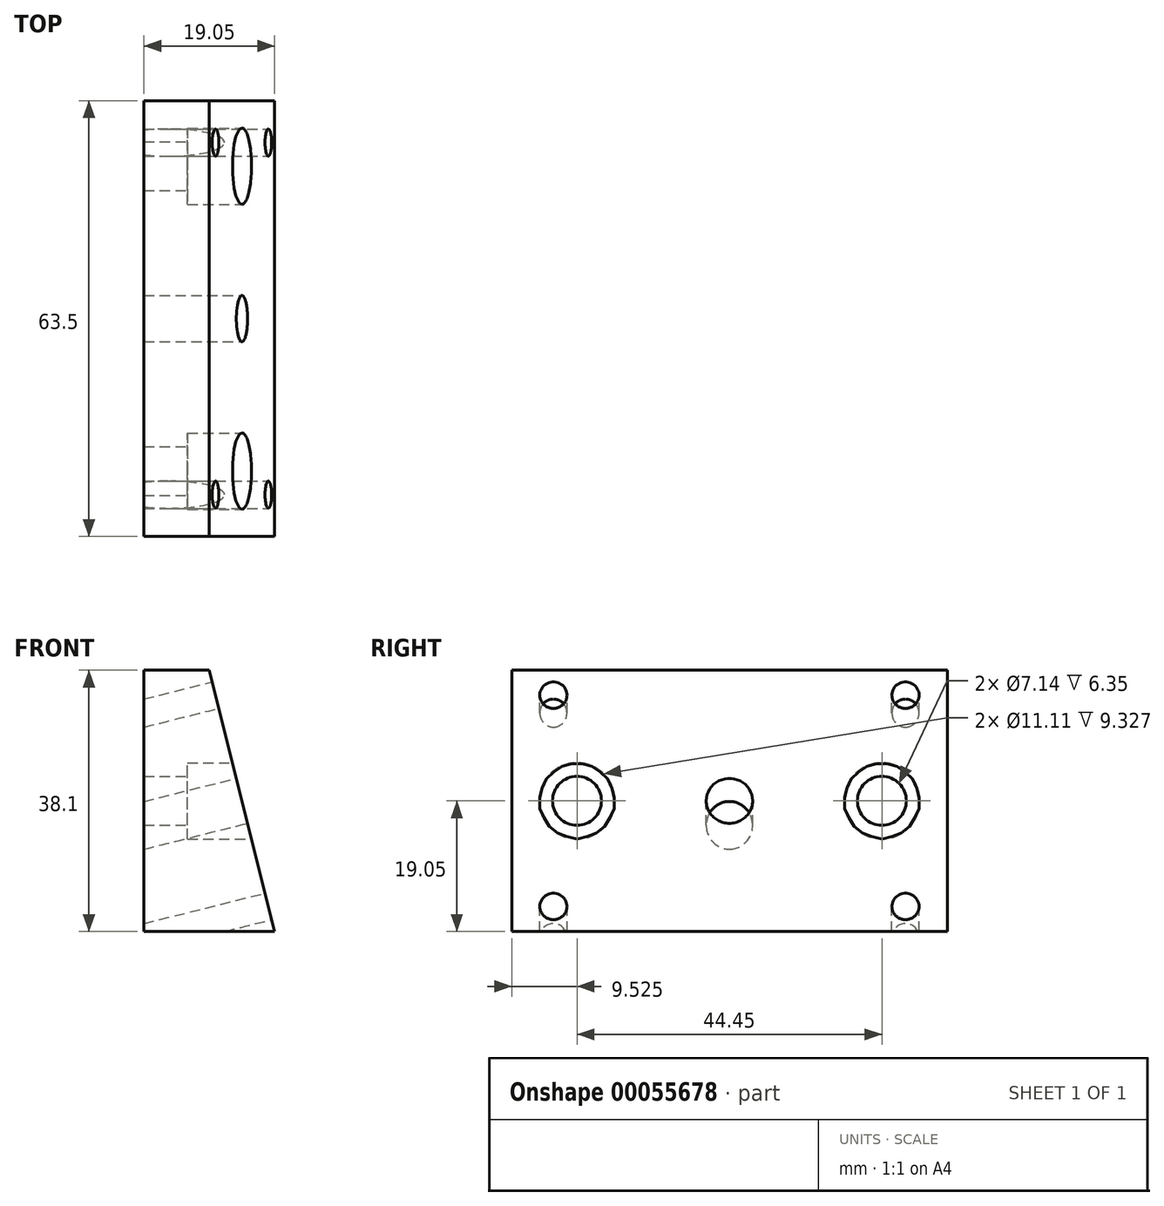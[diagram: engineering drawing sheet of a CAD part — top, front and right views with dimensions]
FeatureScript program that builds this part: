
annotation { "Feature Type Name" : "Feature", "Feature Type Description" : "" }
export const myFeature = defineFeature(function(context is Context, id is Id, definition is map)
    precondition{}
    {
        {
            var Q0;
            Q0=qCreatedBy(makeId("Right.planeOp"),FACE);
            var sketch = newSketch(context, id + "F0", { "sketchPlane" : qUnion([Q0])});
            skLineSegment(sketch, "E0.bottom", {"start": v(0, 0) * mm, "end": v(63.5, 0) * mm});
            skLineSegment(sketch, "E0.top", {"start": v(0, 38.1) * mm, "end": v(63.5, 38.1) * mm});
            skLineSegment(sketch, "E0.left", {"start": v(0, 0) * mm, "end": v(0, 38.1) * mm});
            skLineSegment(sketch, "E0.right", {"start": v(63.5, 0) * mm, "end": v(63.5, 38.1) * mm});
            skSolve(sketch);
        }
        {
            var Q0;
            Q0=makeQuery(id+"F0.imprint","IMPRINT",FACE,{"disambiguationData":[TD([[makeQuery(id+"F0.imprint","IMPRINT",EDGE,{"derivedFrom":sQuery(id+"F0.wireOp",EDGE,"E0.bottom")}),1.0]])]});
            extrude(context, id + "F1", {"entities" : qUnion([Q0]), "depth" : 19.05 * mm});
        }
        {
            var Q0;
            Q0=makeQuery(id+"F1.opExtrude","CAP_FACE",FACE,{"disambiguationData":[OSD([sQuery(id+"F0.wireOp",EDGE,"E0.bottom"),sQuery(id+"F0.wireOp",EDGE,"E0.top"),sQuery(id+"F0.wireOp",EDGE,"E0.left"),sQuery(id+"F0.wireOp",EDGE,"E0.right")])],"isStart":false});
            var sketch = newSketch(context, id + "F2", { "sketchPlane" : qUnion([Q0])});
            skLineSegment(sketch, "E1", {"start": v(0, 19.05) * mm, "end": v(63.5, 19.05) * mm});
            skPoint(sketch, "E2", {"position": v(9.53, 19.05) * mm});
            skPoint(sketch, "E3", {"position": v(53.98, 19.05) * mm});
            skSolve(sketch);
        }
        {
            var Q0;
            Q0=sQuery(id+"F2.wireOp",VERTEX,"E2");
            var Q1;
            Q1=sQuery(id+"F2.wireOp",VERTEX,"E3");
            var Q2;
            Q2=makeQuery(id+"F1.opExtrude","SWEPT_BODY",BODY,{"disambiguationData":[OSD([sQuery(id+"F0.wireOp",EDGE,"E0.bottom"),sQuery(id+"F0.wireOp",EDGE,"E0.top"),sQuery(id+"F0.wireOp",EDGE,"E0.left"),sQuery(id+"F0.wireOp",EDGE,"E0.right")])]});
            hole(context, id + "F3", {"style" : HoleStyle.C_BORE, "holeDiameter" : 7.14 * mm, "cBoreDiameter" : 11.1 * mm, "cBoreDepth" : 12.7 * mm, "endStyle" : HoleEndStyle.THROUGH, "locations" : qUnion([Q0, Q1]), "scope" : qUnion([Q2])});
        }
        {
            var Q0;
            Q0=makeQuery(id+"F1.opExtrude","SWEPT_FACE",FACE,{"disambiguationData":[OSD([sQuery(id+"F0.wireOp",EDGE,"E0.left")])]});
            var sketch = newSketch(context, id + "F4", { "sketchPlane" : qUnion([Q0])});
            skLineSegment(sketch, "E4", {"start": v(9.53, 38.1) * mm, "end": v(19.05, 0) * mm});
            skSolve(sketch);
        }
        {
            var Q0;
            {var subQ0=sQuery(id+"F4.wireOp",EDGE,"E4");Q0=makeQuery(id+"F4.imprint","IMPRINT",FACE,{"disambiguationData":[TD([[makeQuery(id+"F4.imprint","IMPRINT",EDGE,{"derivedFrom":subQ0}),1.0]])]});}
            extrude(context, id + "F5", {"entities" : qUnion([Q0]), "operationType" : NewBodyOperationType.REMOVE, "endBound" : BoundingType.THROUGH_ALL, "oppositeDirection" : true, "depth" : 25.4 * mm});
        }
        {
            var Q0;
            Q0=makeQuery(id+"F5.boolean.opBoolean","COPY",FACE,{"derivedFrom":makeQuery(id+"F5.opExtrude","SWEPT_FACE",FACE,{"disambiguationData":[OSD([sQuery(id+"F4.wireOp",EDGE,"E4")])]})});
            var sketch = newSketch(context, id + "F6", { "sketchPlane" : qUnion([Q0])});
            skLineSegment(sketch, "E5", {"start": v(31.75, 34.65) * mm, "end": v(31.75, -4.62) * mm});
            skPoint(sketch, "E6", {"position": v(31.75, 15.02) * mm});
            skSolve(sketch);
        }
        {
            var Q0;
            Q0=sQuery(id+"F6.wireOp",VERTEX,"E6");
            var Q1;
            Q1=makeQuery(id+"F1.opExtrude","SWEPT_BODY",BODY,{"disambiguationData":[OSD([sQuery(id+"F0.wireOp",EDGE,"E0.bottom"),sQuery(id+"F0.wireOp",EDGE,"E0.top"),sQuery(id+"F0.wireOp",EDGE,"E0.left"),sQuery(id+"F0.wireOp",EDGE,"E0.right")])]});
            hole(context, id + "F7", {"style" : HoleStyle.SIMPLE, "holeDiameter" : 6.76 * mm, "endStyle" : HoleEndStyle.THROUGH, "locations" : qUnion([Q0]), "scope" : qUnion([Q1])});
        }
        {
            var Q0;
            Q0=makeQuery(id+"F5.boolean.opBoolean","COPY",FACE,{"derivedFrom":makeQuery(id+"F5.opExtrude","SWEPT_FACE",FACE,{"disambiguationData":[OSD([sQuery(id+"F4.wireOp",EDGE,"E4")])]})});
            var sketch = newSketch(context, id + "F8", { "sketchPlane" : qUnion([Q0])});
            skLineSegment(sketch, "E7", {"start": v(0, -4.62) * mm, "end": v(63.5, 34.65) * mm});
            skLineSegment(sketch, "E8", {"start": v(0, 34.65) * mm, "end": v(63.5, -4.62) * mm});
            skLineSegment(sketch, "E9.bottom", {"start": v(6.08, 30.9) * mm, "end": v(57.42, 30.9) * mm});
            skLineSegment(sketch, "E9.top", {"start": v(6.08, -0.86) * mm, "end": v(57.42, -0.86) * mm});
            skLineSegment(sketch, "E9.left", {"start": v(6.08, 30.9) * mm, "end": v(6.08, -0.86) * mm});
            skLineSegment(sketch, "E9.right", {"start": v(57.42, 30.9) * mm, "end": v(57.42, -0.86) * mm});
            skPoint(sketch, "E10", {"position": v(31.75, 15.02) * mm});
            skSolve(sketch);
        }
        {
            var Q0;
            Q0=sQuery(id+"F8.wireOp",VERTEX,"E9.left.start");
            var Q1;
            Q1=sQuery(id+"F8.wireOp",VERTEX,"E9.right.start");
            var Q2;
            Q2=sQuery(id+"F8.wireOp",VERTEX,"E9.right.end");
            var Q3;
            Q3=sQuery(id+"F8.wireOp",VERTEX,"E9.left.end");
            var Q4;
            Q4=makeQuery(id+"F1.opExtrude","SWEPT_BODY",BODY,{"disambiguationData":[OSD([sQuery(id+"F0.wireOp",EDGE,"E0.bottom"),sQuery(id+"F0.wireOp",EDGE,"E0.top"),sQuery(id+"F0.wireOp",EDGE,"E0.left"),sQuery(id+"F0.wireOp",EDGE,"E0.right")])]});
            hole(context, id + "F9", {"style" : HoleStyle.SIMPLE, "holeDiameter" : 3.97 * mm, "endStyle" : HoleEndStyle.THROUGH, "locations" : qUnion([Q0, Q1, Q2, Q3]), "scope" : qUnion([Q4])});
        }
    });
